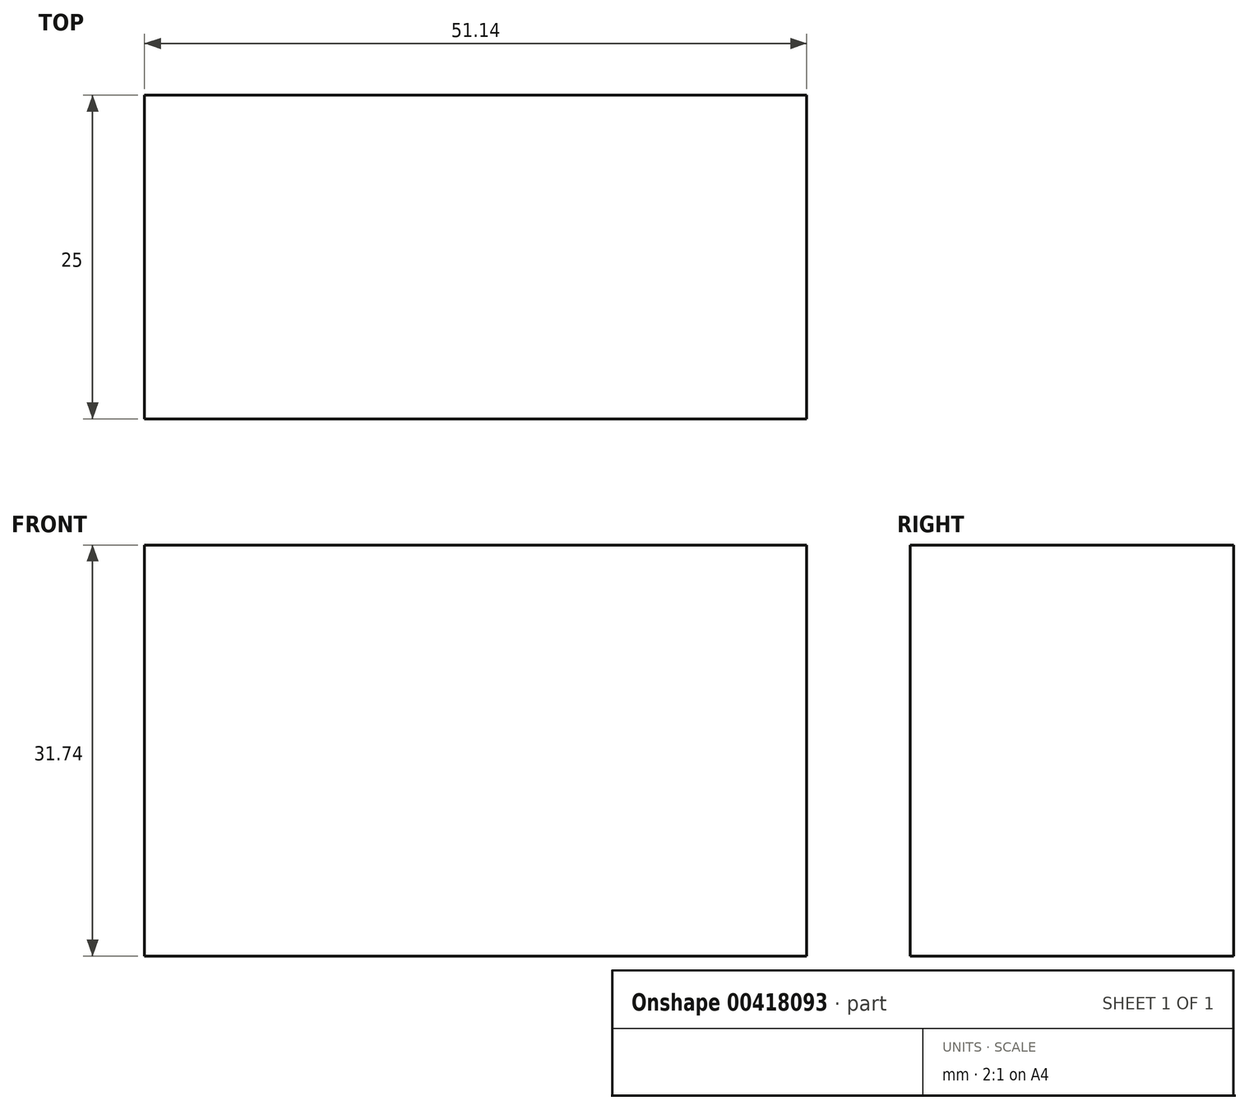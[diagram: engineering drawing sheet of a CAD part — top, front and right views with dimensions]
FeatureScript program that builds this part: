
annotation { "Feature Type Name" : "Feature", "Feature Type Description" : "" }
export const myFeature = defineFeature(function(context is Context, id is Id, definition is map)
    precondition{}
    {
        {
            var Q0;
            Q0=qCreatedBy(makeId("Front.planeOp"),FACE);
            var sketch = newSketch(context, id + "F0", { "sketchPlane" : qUnion([Q0])});
            skCircle(sketch, "E0", {"center": v(-61.08, 59.52) * mm, "radius": 22.5 * mm});
            skLineSegment(sketch, "E1.bottom", {"start": v(-51.14, 48.94) * mm, "end": v(0, 48.94) * mm});
            skLineSegment(sketch, "E1.top", {"start": v(-51.14, 17.2) * mm, "end": v(0, 17.2) * mm});
            skLineSegment(sketch, "E1.left", {"start": v(-51.14, 48.94) * mm, "end": v(-51.14, 17.2) * mm});
            skLineSegment(sketch, "E1.right", {"start": v(0, 48.94) * mm, "end": v(0, 17.2) * mm});
            skSolve(sketch);
        }
        {
            var Q0;
            {var subQ1=sQuery(id+"F0.wireOp",EDGE,"E1.top");Q0=makeQuery(id+"F0.imprint","IMPRINT",FACE,{"disambiguationData":[TD([[makeQuery(id+"F0.imprint","IMPRINT",EDGE,{"derivedFrom":subQ1}),1.0]])]});}
            var Q1;
            {var subQ0=sQuery(id+"F0.wireOp",EDGE,"E1.bottom");var subQ1=sQuery(id+"F0.wireOp",EDGE,"E0");var subQ2=makeQuery(id+"F0.imprint","INTERSECT",VERTEX,{"derivedFrom":[subQ1,subQ0]});Q1=makeQuery(id+"F0.imprint","IMPRINT",FACE,{"disambiguationData":[TD([[makeQuery(id+"F0.imprint","IMPRINT",EDGE,{"disambiguationData":[TD([[subQ2,1.0]])],"derivedFrom":subQ1}),1.0]])]});}
            extrude(context, id + "F1", {"entities" : qUnion([Q0, Q1]), "depth" : 25 * mm});
        }
    });
